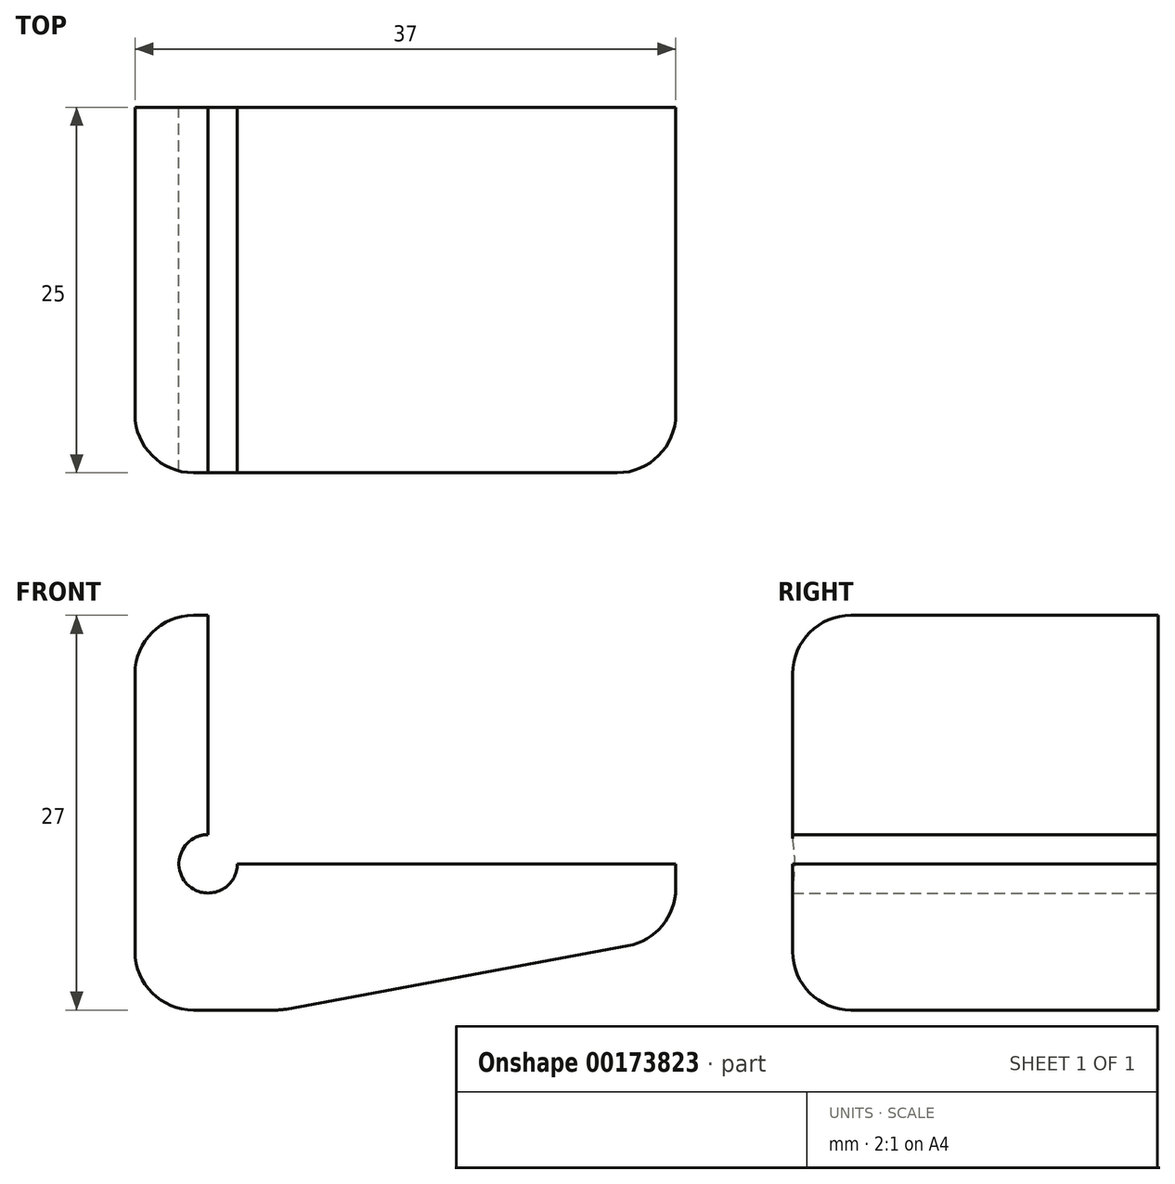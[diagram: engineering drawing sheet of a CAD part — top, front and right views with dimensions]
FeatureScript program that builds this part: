
annotation { "Feature Type Name" : "Feature", "Feature Type Description" : "" }
export const myFeature = defineFeature(function(context is Context, id is Id, definition is map)
    precondition{}
    {
        {
            var Q0;
            Q0=qCreatedBy(makeId("Front.planeOp"),FACE);
            var sketch = newSketch(context, id + "F0", { "sketchPlane" : qUnion([Q0])});
            skLineSegment(sketch, "E0", {"start": v(2, 0) * mm, "end": v(32, 0) * mm});
            skLineSegment(sketch, "E1", {"start": v(0, 17) * mm, "end": v(0, 2) * mm});
            skLineSegment(sketch, "E2", {"start": v(0, 17) * mm, "end": v(-1, 17) * mm});
            skLineSegment(sketch, "E3", {"start": v(-5, 13) * mm, "end": v(-5, -6) * mm});
            skLineSegment(sketch, "E4", {"start": v(-1, -10) * mm, "end": v(4.63, -10) * mm});
            skLineSegment(sketch, "E5", {"start": v(5.36, -9.93) * mm, "end": v(28.73, -5.6) * mm});
            skLineSegment(sketch, "E6", {"start": v(32, -1.67) * mm, "end": v(32, 0) * mm});
            skArc(sketch, "E7", {"start": v(0, 2) * mm, "mid": v(-1.41, -1.41) * mm, "end": v(2, 0) * mm});
            skPoint(sketch, "E8.visualSharp", {"position": v(-5, 17) * mm});
            skArc(sketch, "E8.filletArc", {"start": v(-1, 17) * mm, "mid": v(-3.83, 15.83) * mm, "end": v(-5, 13) * mm});
            skPoint(sketch, "E9.visualSharp", {"position": v(-5, -10) * mm});
            skArc(sketch, "E9.filletArc", {"start": v(-5, -6) * mm, "mid": v(-3.83, -8.83) * mm, "end": v(-1, -10) * mm});
            skPoint(sketch, "E10.visualSharp", {"position": v(5, -10) * mm});
            skArc(sketch, "E10.filletArc", {"start": v(4.63, -10) * mm, "mid": v(5, -9.98) * mm, "end": v(5.36, -9.93) * mm});
            skPoint(sketch, "E11.visualSharp", {"position": v(32, -5) * mm});
            skArc(sketch, "E11.filletArc", {"start": v(28.73, -5.6) * mm, "mid": v(31.08, -4.23) * mm, "end": v(32, -1.67) * mm});
            skSolve(sketch);
        }
        {
            var Q0;
            Q0=makeQuery(id+"F0.imprint","IMPRINT",FACE,{"disambiguationData":[TD([[makeQuery(id+"F0.imprint","IMPRINT",EDGE,{"derivedFrom":sQuery(id+"F0.wireOp",EDGE,"E0")}),-1.0]])]});
            extrude(context, id + "F1", {"entities" : qUnion([Q0]), "depth" : 25 * mm, "offsetDistance" : 25 * mm});
        }
        {
            var Q0;
            Q0=makeQuery(id+"F1.opExtrude","CAP_EDGE",EDGE,{"disambiguationData":[OSD([sQuery(id+"F0.wireOp",EDGE,"E3")])],"isStart":false});
            fillet(context, id + "F2", {"entities" : qUnion([Q0]), "tangentPropagation" : true, "radius" : 4 * mm, "defaultsChanged" : false, "vertexSettings" : [], "allowEdgeOverflow" : false});
        }
    });
